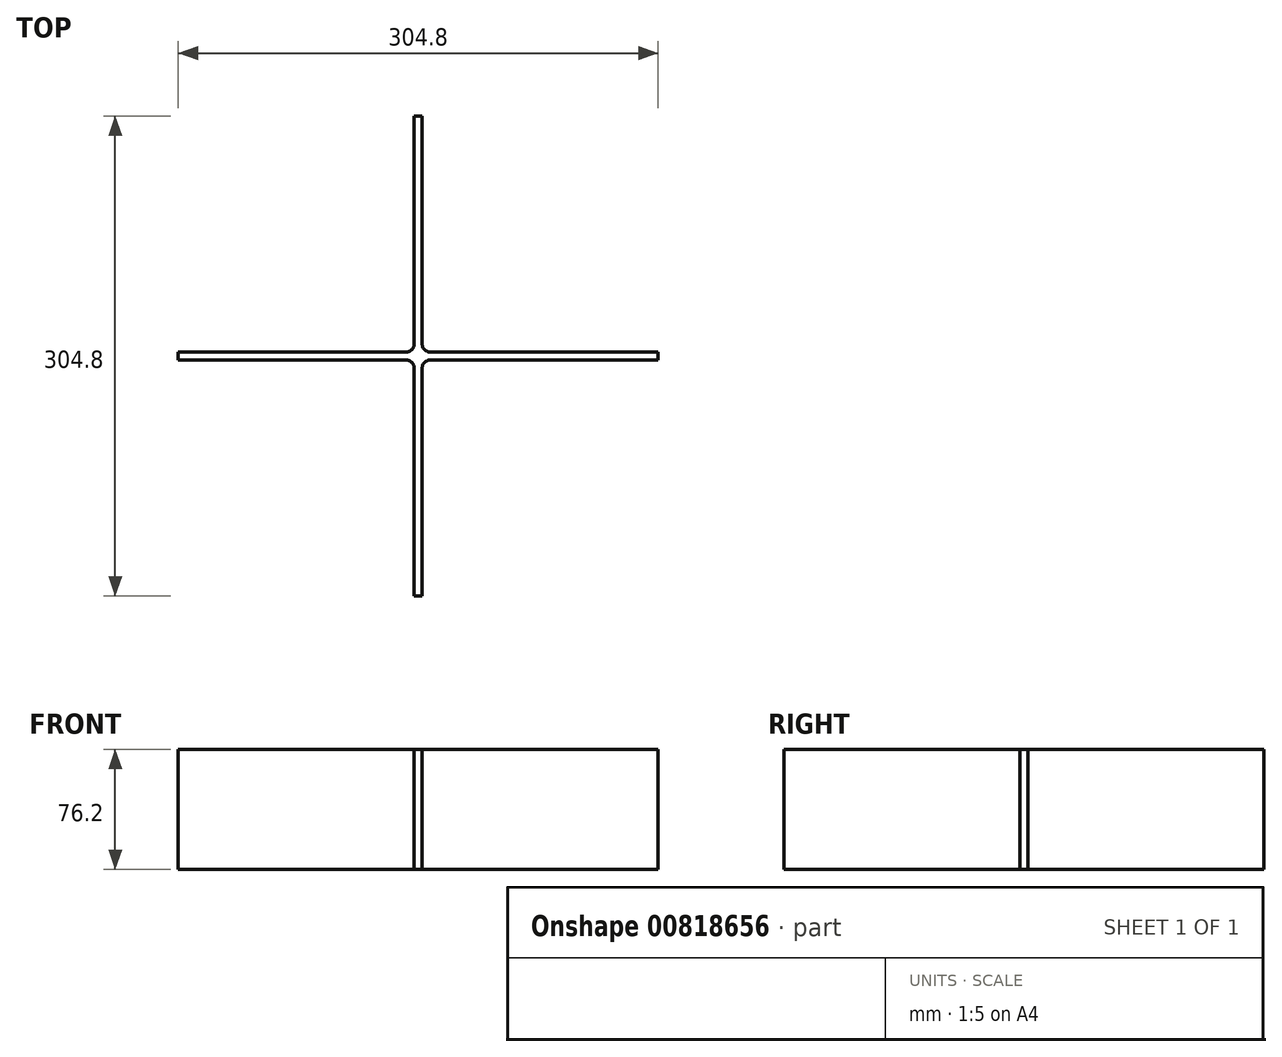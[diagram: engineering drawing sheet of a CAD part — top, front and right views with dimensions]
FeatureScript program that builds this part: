
annotation { "Feature Type Name" : "Feature", "Feature Type Description" : "" }
export const myFeature = defineFeature(function(context is Context, id is Id, definition is map)
    precondition{}
    {
        {
            var Q0;
            Q0=qCreatedBy(makeId("Top.planeOp"),FACE);
            var sketch = newSketch(context, id + "F0", { "sketchPlane" : qUnion([Q0])});
            skLineSegment(sketch, "E0.bottom", {"start": v(0, 0) * mm, "end": v(304.8, 0) * mm});
            skLineSegment(sketch, "E0.top", {"start": v(0, -5.08) * mm, "end": v(304.8, -5.08) * mm});
            skLineSegment(sketch, "E0.left", {"start": v(0, 0) * mm, "end": v(0, -5.08) * mm});
            skLineSegment(sketch, "E0.right", {"start": v(304.8, 0) * mm, "end": v(304.8, -5.08) * mm});
            skLineSegment(sketch, "E1", {"start": v(152.4, 0) * mm, "end": v(152.4, -5.08) * mm});
            skLineSegment(sketch, "E2.bottom", {"start": v(154.94, -154.94) * mm, "end": v(149.86, -154.94) * mm});
            skLineSegment(sketch, "E2.top", {"start": v(154.94, 149.86) * mm, "end": v(149.86, 149.86) * mm});
            skLineSegment(sketch, "E2.left", {"start": v(154.94, -154.94) * mm, "end": v(154.94, 149.86) * mm});
            skLineSegment(sketch, "E2.right", {"start": v(149.86, -154.94) * mm, "end": v(149.86, 149.86) * mm});
            skPoint(sketch, "E2.middle", {"position": v(152.4, -2.54) * mm});
            skSolve(sketch);
        }
        {
            var Q0;
            {var subQ0=sQuery(id+"F0.wireOp",EDGE,"E0.left");Q0=makeQuery(id+"F0.imprint","IMPRINT",FACE,{"disambiguationData":[TD([[makeQuery(id+"F0.imprint","IMPRINT",EDGE,{"derivedFrom":subQ0}),1.0]])]});}
            var Q1;
            {var subQ1=sQuery(id+"F0.wireOp",EDGE,"E2.top");Q1=makeQuery(id+"F0.imprint","IMPRINT",FACE,{"disambiguationData":[TD([[makeQuery(id+"F0.imprint","IMPRINT",EDGE,{"derivedFrom":subQ1}),1.0]])]});}
            var Q2;
            {var subQ0=sQuery(id+"F0.wireOp",EDGE,"E0.right");Q2=makeQuery(id+"F0.imprint","IMPRINT",FACE,{"disambiguationData":[TD([[makeQuery(id+"F0.imprint","IMPRINT",EDGE,{"derivedFrom":subQ0}),-1.0]])]});}
            var Q3;
            {var subQ0=sQuery(id+"F0.wireOp",EDGE,"E1");Q3=makeQuery(id+"F0.imprint","IMPRINT",FACE,{"disambiguationData":[TD([[makeQuery(id+"F0.imprint","IMPRINT",EDGE,{"derivedFrom":subQ0}),-1.0]])]});}
            var Q4;
            {var subQ0=sQuery(id+"F0.wireOp",EDGE,"E1");Q4=makeQuery(id+"F0.imprint","IMPRINT",FACE,{"disambiguationData":[TD([[makeQuery(id+"F0.imprint","IMPRINT",EDGE,{"derivedFrom":subQ0}),1.0]])]});}
            var Q5;
            {var subQ1=sQuery(id+"F0.wireOp",EDGE,"E2.bottom");Q5=makeQuery(id+"F0.imprint","IMPRINT",FACE,{"disambiguationData":[TD([[makeQuery(id+"F0.imprint","IMPRINT",EDGE,{"derivedFrom":subQ1}),-1.0]])]});}
            extrude(context, id + "F1", {"entities" : qUnion([Q0, Q1, Q2, Q3, Q4, Q5]), "depth" : 76.2 * mm, "offsetDistance" : 25.4 * mm});
        }
        {
            var Q0;
            Q0=makeQuery(id+"F1.opExtrude","SWEPT_EDGE",EDGE,{"disambiguationData":[OSD([sQuery(id+"F0.wireOp",EDGE,"E0.top"),sQuery(id+"F0.wireOp",EDGE,"E2.right")])]});
            var Q1;
            Q1=makeQuery(id+"F1.opExtrude","SWEPT_EDGE",EDGE,{"disambiguationData":[OSD([sQuery(id+"F0.wireOp",EDGE,"E0.top"),sQuery(id+"F0.wireOp",EDGE,"E2.left")])]});
            var Q2;
            Q2=makeQuery(id+"F1.opExtrude","SWEPT_EDGE",EDGE,{"disambiguationData":[OSD([sQuery(id+"F0.wireOp",EDGE,"E0.bottom"),sQuery(id+"F0.wireOp",EDGE,"E2.left")])]});
            var Q3;
            Q3=makeQuery(id+"F1.opExtrude","SWEPT_EDGE",EDGE,{"disambiguationData":[OSD([sQuery(id+"F0.wireOp",EDGE,"E0.bottom"),sQuery(id+"F0.wireOp",EDGE,"E2.right")])]});
            fillet(context, id + "F2", {"entities" : qUnion([Q0, Q1, Q2, Q3]), "radius" : 5.08 * mm, "tangentPropagation" : true, "allowEdgeOverflow" : false});
        }
    });
